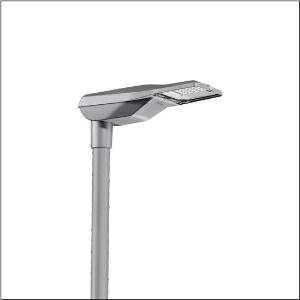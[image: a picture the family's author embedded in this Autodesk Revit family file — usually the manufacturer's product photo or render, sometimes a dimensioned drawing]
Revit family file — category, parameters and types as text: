
# Revit family: streetlight_sl_21_iq_micro___st1_0a_5xe1d31g08cb_12bc
name_source: partatom
category: Lighting Fixtures
units: mm (PartAtom-declared; Revit-internal decimal feet)

## family parameters
Cut with Voids When Loaded = No
Host = Face
Light Source = No
Part Type = Normal
Room Calculation Point = No
Round Connector Dimension = Use Diameter
Shared = No

## types (1)
- --- (1 x LED, 2870 lm, 19.4 W, 3000K)
    Apparent Load = 19 VA
    CIE Flux Codes = 37 72 97 100 100
    Color Rendering = 70
    Color Temperature = 3000K
    Default Elevation = 1800 mm
    Description = Streetlight SL 21 iQ micro, mast luminaire, primary light control with lens, of PMMA, primary optical cover: cover, of toughened safety glass, transparent, light distribution: ST1.0a, light emission: direct distribution, primary light characteristic: asymmetric, installation type: post-top, side-entry, LED, High Power LED, rated luminous flux: 2.870lm, luminous efficacy: 148lm/W, light colour: 730, colour temperature: 3000K, control: Street-Remote, Auto-Match, Temp-Guard, Lumen-Switch, Night-Set, Smart-Wire, Light-Fading, Desk-Remote (wireless, voltage-free reading and setting of iQ features in the workshop via application-optimized NFC function/RFID function), optimised constant luminous flux control (CLO 2.0), presetting dimming linear, mains connection: 220..240V, AC, 50/60Hz, start of lifetime: 19W, end of service life: 20W, reduction: 10W, luminaire housing, of diecast aluminium, powder-coated, Siteco® metallic grey (DB 702S), corrosivity category C5 mid according to DIN EN ISO 12944, please order mast flange separately, inclination adjustable: 0°, 5°, 10°, 15°, sealing non-destructively replaceable, multi-level sealing system, length: 528mm, width: 235mm, height: 110mm, mast flange for spigot size: 42mm (side-entry): 5XC10008XM4, 60/48mm (side-entry/post-top): 5XC10108XM2, 76/60mm (side-entry/post-top): 5XC10108XM1, protection rating (complete): IP66, insulation class (complete): insulation class II (safety insulation), certification: CE, ENEC, ENEC+, VDE, impact resistance: IK09, permissible operating ambient temperature for outdoor applications: -40..+50°C, standard-compliant lighting for roads and squares, packaging unit: 1 piece

Light Distribution: ST1.0a
    Height = 110 mm
    Lamp = 1 x LED
    Lamp Light Flux = 2870 lm
    Lamp Power = 19.4 W
    Lamp count = 1
    Length = 528 mm
    Luminous efficacy = 148 lm/W
    Manufacturer = Siteco
    ModVariant = No
    Model = 5XE1D31G08CB
    Number of Poles = 1
    OnlyDefault = Yes
    Power Factor = 1
    Product Name = Streetlight SL 21 iQ micro | ST1.0a
    Product group = mast luminaire | pylon top
    ProductGroupID = 6100
    Protection Class = Protection class II
    Protection Degree = IP 66
    RLX_Detail_Level = 1
    RLX_Emergency_Light_Flux = 0 lm
    RLX_Emergency_Type = 0
    RLX_Emergency_Type_DB = No
    RlxData = <blob elided: 98541 chars, md5=7c2f4095>
    Socket = socket
    Standby Power = 0 W
    System Light Flux = 2870 lm
    System Power = 19 W
    Type Comments = factory setting: luminous flux: 100 % | dim-lin: 254 | 387 mA
    Type Image = l_1006881.jpg
    URL = http://relux.com
    VarID = @adj_088621
    Voltage = 0 V
    Weight = 0.00 kg
    Width = 235 mm

## geometry (parser evidence)
native form markers: Blend x4, Sweep x11
no freeform markers — native parametric forms only
